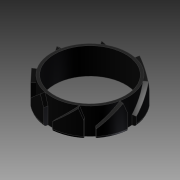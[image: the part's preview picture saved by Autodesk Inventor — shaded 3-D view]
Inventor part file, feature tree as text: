
AUTODESK INVENTOR PART (.ipt)
format: ipt  version: 2012 (Build 160160000, 160)  size: 248,832 bytes
history: native  units: mm
features: sketch x4, extrude x2, pattern_circular x2, helix x2, fillet x1
ambient origin geometry x8: Origin, YZ Plane, XZ Plane, XY Plane, X Axis, Y Axis, Z Axis, Center Point
bodies: Solid1 (feature_tree)
feature tree (11):
  sketch  "Sketch1"  dims[d0=64.0mm d1=54.0mm d2=50.0mm]
  extrude  "Extrusion2"  Depth=54.0mm
  sketch  "Sketch3"  dims[d3=58.0mm d6=20.0mm d7=0.0mm]
  fillet  "Fillet3"  Radius=50.0mm
  sketch  "Sketch5"  dims[d10=4.0mm]
  extrude  "Extrusion9"  Depth=20.0mm TaperAngle=0.0deg
  pattern_circular  "Circular Pattern6"  [2 undecoded]
  sketch  "Sketch7"  dims[d17=2.0mm d35=44.1mm d36=55.0mm d37=1.012291mm d46=2.0mm d47=4.0mm d58=4.0mm d59=26.0mm d86=2.094395mm d87=10.0mm d88=0.0mm d89=80.0mm d90=360.0deg d92=1.047198mm d93=29.0mm d94=22.0mm d95=10.0mm d96=16.0mm d97=0.9375mm d98=0.0mm d99=90.0deg d100=90.0deg d101=0.0mm d102=0.0mm d103=16.0mm d104=10.0mm d105=16.0mm d106=0.3125mm d107=0.0mm d108=90.0deg d109=90.0deg d110=0.0mm d111=0.0mm d112=80.0mm d113=360.0deg d115=18.0mm]
  helix  "Coil5"  [1 undecoded]
  helix  "Coil6"  [1 undecoded]
  pattern_circular  "Circular Pattern7"  [2 undecoded]
note: 6 required parameter values undecoded (feature->parameter linkage not recoverable at this tier; creation-order binding heuristic only, values carry confidence <= 0.55)
